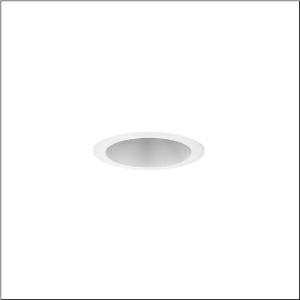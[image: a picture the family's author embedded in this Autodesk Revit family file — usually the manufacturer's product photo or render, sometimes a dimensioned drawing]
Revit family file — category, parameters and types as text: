
# Revit family: lunis_31-l_51dn16ee41b
name_source: partatom
category: Lighting Fixtures
units: mm (PartAtom-declared; Revit-internal decimal feet)

## family parameters
Cut with Voids When Loaded = No
Host = Face
Light Source = No
Part Type = Normal
Room Calculation Point = No
Round Connector Dimension = Use Diameter
Shared = No

## types (1)
- --- (1 x LED, 1600 lm, 12 W, 4000K)
    Apparent Load = 12 VA
    CIE Flux Codes = 76 93 99 100 100
    Color Rendering = 80
    Color Temperature = 4000K
    Default Elevation = 1800 mm
    Description = Lunis 31-L, downlight, light control with reflector, light emission: direct distribution, LED rated luminous flux: 1.600lm, light colour: 840, mains connection: 220..240V, AC/DC, 0/50..60Hz, housing, of aluminium, white, protection rating (complete): IP20, protection rating (on room side): IP54, insulation class (complete): insulation class II (safety insulation), certification: CE, ENEC, packaging unit: 1 piece
    Height = 0 mm  [stored 0 ft]
    Lamp = 1 x LED
    Lamp Light Flux = 1600 lm
    Lamp Power = 12 W
    Lamp count = 1
    Length = 188 mm  [stored 0.616798 ft]
    Luminous efficacy = 133 lm/W
    Manufacturer = Siteco
    ModVariant = No
    Model = 51DN16EE41B
    Mounting Place = Ceiling
    Mounting Type = Recessed
    Number of Poles = 1
    OnlyDefault = Yes
    Power Factor = 1
    Product Name = Lunis 31-L
    Product group = downlight
    ProductGroupID = 401
    Protection Class = Protection class II
    Protection Degree = IP 20
    RLX_Detail_Level = 1
    RLX_Emergency_Light_Flux = 0 lm
    RLX_Emergency_Type = 0
    RLX_Emergency_Type_DB = No
    RlxData = <blob elided: 22553 chars, md5=e2e644b6>
    Socket = socket
    Standby Power = 0 W
    System Light Flux = 1600 lm
    System Power = 12 W
    Type Comments = individual setting: luminous flux: 100 % | (OFF | ON) | 300 mA
    Type Image = l_1345911.jpg
    URL = http://relux.com
    VarID = @adj_031465
    Voltage = 0 V
    Weight = 0.00 kg
    Width = 0 mm  [stored 0 ft]

note: [stored X ft] marks values corroborated as IEEE doubles in the binary element streams (Revit-internal decimal feet)

## geometry (parser evidence)
native form markers: Blend x4, Sweep x9
no freeform markers — native parametric forms only
